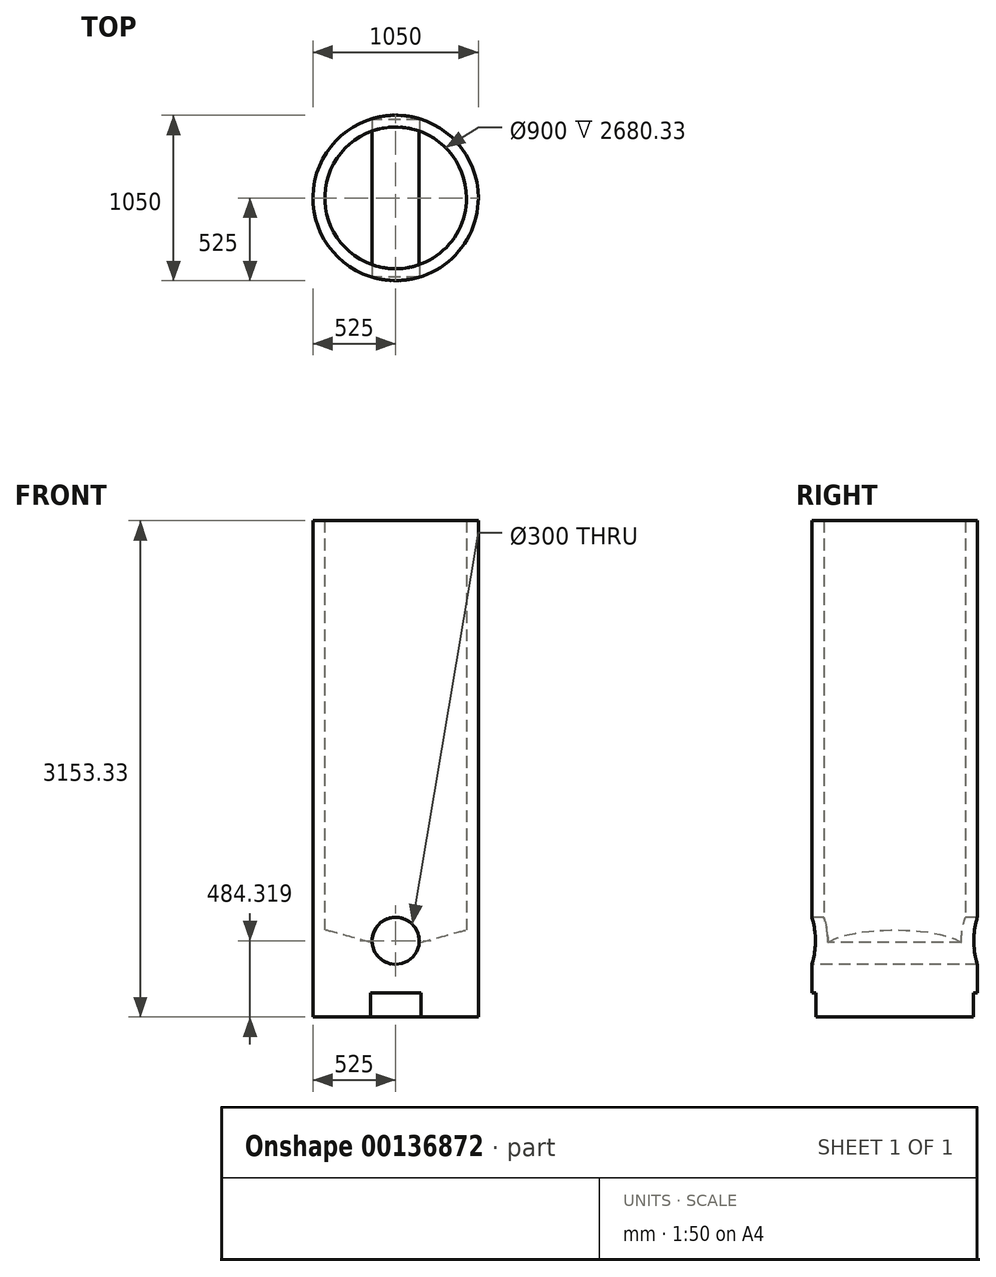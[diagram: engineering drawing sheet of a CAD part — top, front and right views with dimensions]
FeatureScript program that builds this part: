
annotation { "Feature Type Name" : "Feature", "Feature Type Description" : "" }
export const myFeature = defineFeature(function(context is Context, id is Id, definition is map)
    precondition{}
    {
        {
            var Q0;
            Q0=qCreatedBy(makeId("Top.planeOp"),FACE);
            var sketch = newSketch(context, id + "F0", { "sketchPlane" : qUnion([Q0])});
            skCircle(sketch, "E0", {"center": v(0, 0) * mm, "radius": 450 * mm});
            skCircle(sketch, "E1", {"center": v(0, 0) * mm, "radius": 525 * mm});
            skSolve(sketch);
        }
        {
            var Q0;
            Q0=makeQuery(id+"F0.imprint","IMPRINT",FACE,{"disambiguationData":[TD([[makeQuery(id+"F0.imprint","IMPRINT",EDGE,{"derivedFrom":sQuery(id+"F0.wireOp",EDGE,"E0")}),-1.0]])]});
            extrude(context, id + "F1", {"entities" : qUnion([Q0]), "depth" : 3000 * mm});
        }
        {
            var Q0;
            Q0=qCreatedBy(makeId("Front.planeOp"),FACE);
            var sketch = newSketch(context, id + "F2", { "sketchPlane" : qUnion([Q0])});
            skLineSegment(sketch, "E2", {"start": v(0, 279.6) * mm, "end": v(-736.25, 476.87) * mm});
            skLineSegment(sketch, "E3", {"start": v(-736.25, 476.87) * mm, "end": v(-736.25, -153.33) * mm});
            skLineSegment(sketch, "E4", {"start": v(-736.25, -153.33) * mm, "end": v(736.25, -153.33) * mm});
            skLineSegment(sketch, "E5", {"start": v(736.25, -153.33) * mm, "end": v(736.25, 476.87) * mm});
            skLineSegment(sketch, "E6", {"start": v(736.25, 476.87) * mm, "end": v(0, 279.6) * mm});
            skSolve(sketch);
        }
        {
            var Q0;
            Q0=makeQuery(id+"F2.imprint","IMPRINT",FACE,{"disambiguationData":[TD([[makeQuery(id+"F2.imprint","IMPRINT",EDGE,{"derivedFrom":sQuery(id+"F2.wireOp",EDGE,"E2")}),1.0]])]});
            extrude(context, id + "F3", {"entities" : qUnion([Q0]), "operationType" : NewBodyOperationType.ADD, "endBound" : BoundingType.SYMMETRIC, "depth" : 1000 * mm});
        }
        {
            var Q0;
            Q0=makeQuery(id+"F1.opExtrude","CAP_FACE",FACE,{"disambiguationData":[OSD([sQuery(id+"F0.wireOp",EDGE,"E0"),sQuery(id+"F0.wireOp",EDGE,"E1")])],"isStart":false});
            var sketch = newSketch(context, id + "F4", { "sketchPlane" : qUnion([Q0])});
            skCircle(sketch, "E7", {"center": v(0, 0) * mm, "radius": 525 * mm});
            skLineSegment(sketch, "E8.bottom", {"start": v(-779.95, 646.9) * mm, "end": v(869.6, 646.9) * mm});
            skLineSegment(sketch, "E8.top", {"start": v(-779.95, -608.91) * mm, "end": v(869.6, -608.91) * mm});
            skLineSegment(sketch, "E8.left", {"start": v(-779.95, 646.9) * mm, "end": v(-779.95, -608.91) * mm});
            skLineSegment(sketch, "E8.right", {"start": v(869.6, 646.9) * mm, "end": v(869.6, -608.91) * mm});
            skSolve(sketch);
        }
        {
            var Q0;
            Q0=makeQuery(id+"F4.imprint","IMPRINT",FACE,{"disambiguationData":[TD([[makeQuery(id+"F4.imprint","IMPRINT",EDGE,{"derivedFrom":sQuery(id+"F4.wireOp",EDGE,"E7")}),-1.0]])]});
            extrude(context, id + "F5", {"entities" : qUnion([Q0]), "operationType" : NewBodyOperationType.REMOVE, "oppositeDirection" : true, "depth" : 7000 * mm});
        }
        {
            var Q0;
            Q0=qCreatedBy(makeId("Front.planeOp"),FACE);
            var sketch = newSketch(context, id + "F6", { "sketchPlane" : qUnion([Q0])});
            skCircle(sketch, "E9", {"center": v(0, 330.99) * mm, "radius": 150 * mm});
            skSolve(sketch);
        }
        {
            var Q0;
            Q0 = qSketchRegion(id + "F6", true);
            extrude(context, id + "F7", {"entities" : qUnion([Q0]), "operationType" : NewBodyOperationType.REMOVE, "endBound" : BoundingType.SYMMETRIC, "oppositeDirection" : true, "depth" : 1100 * mm});
        }
    });
